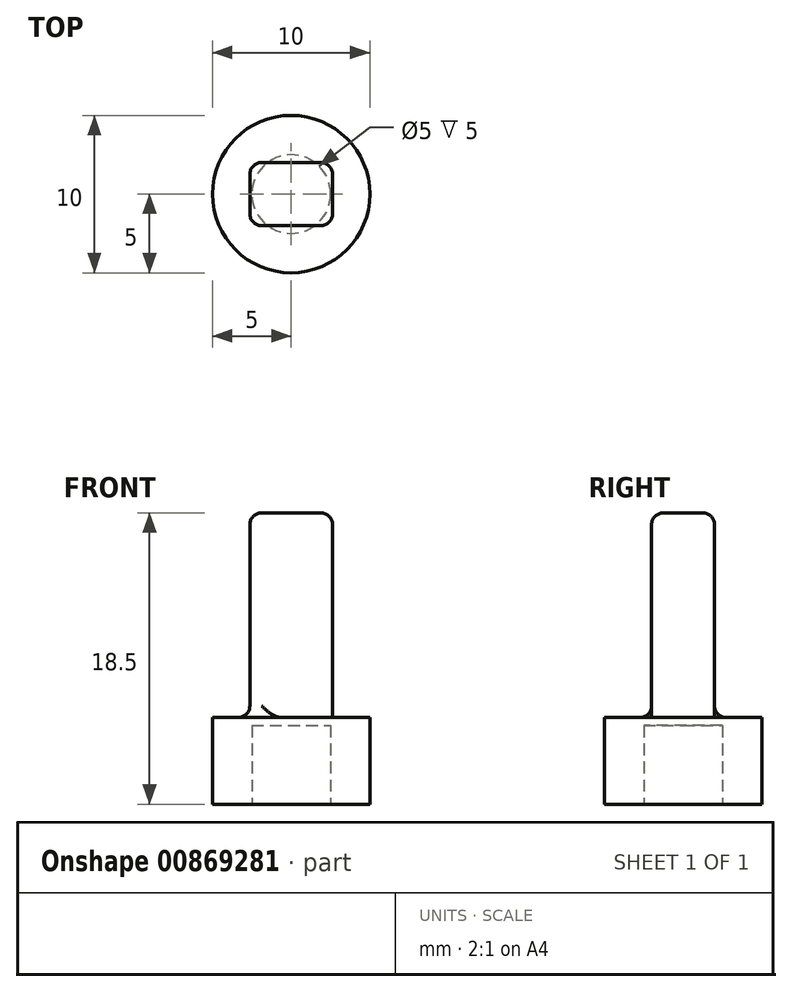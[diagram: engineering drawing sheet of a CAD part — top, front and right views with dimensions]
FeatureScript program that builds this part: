
annotation { "Feature Type Name" : "Feature", "Feature Type Description" : "" }
export const myFeature = defineFeature(function(context is Context, id is Id, definition is map)
    precondition{}
    {
        {
            var Q0;
            Q0=qCreatedBy(makeId("Top.planeOp"),FACE);
            var sketch = newSketch(context, id + "F0", { "sketchPlane" : qUnion([Q0])});
            skCircle(sketch, "E0", {"center": v(0, 0) * mm, "radius": 5 * mm});
            skSolve(sketch);
        }
        {
            var Q0;
            Q0=makeQuery(id+"F0.imprint","IMPRINT",FACE,{"disambiguationData":[TD([[makeQuery(id+"F0.imprint","IMPRINT",EDGE,{"derivedFrom":sQuery(id+"F0.wireOp",EDGE,"E0")}),1.0]])]});
            extrude(context, id + "F1", {"entities" : qUnion([Q0]), "depth" : 5.5 * mm, "offsetDistance" : 25 * mm});
        }
        {
            var Q0;
            Q0=makeQuery(id+"F1.opExtrude","CAP_FACE",FACE,{"disambiguationData":[OSD([sQuery(id+"F0.wireOp",EDGE,"E0")])],"isStart":false});
            var sketch = newSketch(context, id + "F2", { "sketchPlane" : qUnion([Q0])});
            skLineSegment(sketch, "E1.bottom", {"start": v(2.62, -2) * mm, "end": v(-2.62, -2) * mm});
            skLineSegment(sketch, "E1.top", {"start": v(2.62, 2) * mm, "end": v(-2.62, 2) * mm});
            skLineSegment(sketch, "E1.left", {"start": v(2.62, -2) * mm, "end": v(2.62, 2) * mm});
            skLineSegment(sketch, "E1.right", {"start": v(-2.62, -2) * mm, "end": v(-2.62, 2) * mm});
            skPoint(sketch, "E1.middle", {"position": v(0, 0) * mm});
            skSolve(sketch);
        }
        {
            var Q0;
            Q0 = qSketchRegion(id + "F2", true);
            extrude(context, id + "F3", {"entities" : qUnion([Q0]), "operationType" : NewBodyOperationType.ADD, "depth" : 13 * mm, "offsetDistance" : 25 * mm});
        }
        {
            var Q0;
            Q0=makeQuery(id+"F3.opExtrude","SWEPT_EDGE",EDGE,{"disambiguationData":[OSD([sQuery(id+"F2.wireOp",EDGE,"E1.bottom"),sQuery(id+"F2.wireOp",EDGE,"E1.right")])]});
            var Q1;
            Q1=makeQuery(id+"F3.opExtrude","SWEPT_EDGE",EDGE,{"disambiguationData":[OSD([sQuery(id+"F2.wireOp",EDGE,"E1.bottom"),sQuery(id+"F2.wireOp",EDGE,"E1.left")])]});
            var Q2;
            Q2=makeQuery(id+"F3.opExtrude","SWEPT_EDGE",EDGE,{"disambiguationData":[OSD([sQuery(id+"F2.wireOp",EDGE,"E1.top"),sQuery(id+"F2.wireOp",EDGE,"E1.left")])]});
            var Q3;
            Q3=makeQuery(id+"F3.opExtrude","SWEPT_FACE",FACE,{"disambiguationData":[OSD([sQuery(id+"F2.wireOp",EDGE,"E1.right")])]});
            var Q4;
            Q4=makeQuery(id+"F3.opExtrude","CAP_EDGE",EDGE,{"disambiguationData":[OSD([sQuery(id+"F2.wireOp",EDGE,"E1.bottom")])],"isStart":false});
            var Q5;
            Q5=makeQuery(id+"F3.opExtrude","CAP_EDGE",EDGE,{"disambiguationData":[OSD([sQuery(id+"F2.wireOp",EDGE,"E1.left")])],"isStart":false});
            var Q6;
            Q6=makeQuery(id+"F3.opExtrude","CAP_EDGE",EDGE,{"disambiguationData":[OSD([sQuery(id+"F2.wireOp",EDGE,"E1.top")])],"isStart":false});
            fillet(context, id + "F4", {"entities" : qUnion([Q0, Q1, Q2, Q3, Q4, Q5, Q6]), "radius" : .75 * mm, "tangentPropagation" : true, "allowEdgeOverflow" : false});
        }
        {
            var Q0;
            Q0=makeQuery(id+"F1.opExtrude","CAP_FACE",FACE,{"disambiguationData":[OSD([sQuery(id+"F0.wireOp",EDGE,"E0")])],"isStart":true});
            var sketch = newSketch(context, id + "F5", { "sketchPlane" : qUnion([Q0])});
            skCircle(sketch, "E2", {"center": v(0, 0) * mm, "radius": 2.5 * mm});
            skSolve(sketch);
        }
        {
            var Q0;
            Q0 = qSketchRegion(id + "F5", true);
            extrude(context, id + "F6", {"entities" : qUnion([Q0]), "operationType" : NewBodyOperationType.REMOVE, "oppositeDirection" : true, "depth" : 5 * mm, "offsetDistance" : 25 * mm});
        }
    });
